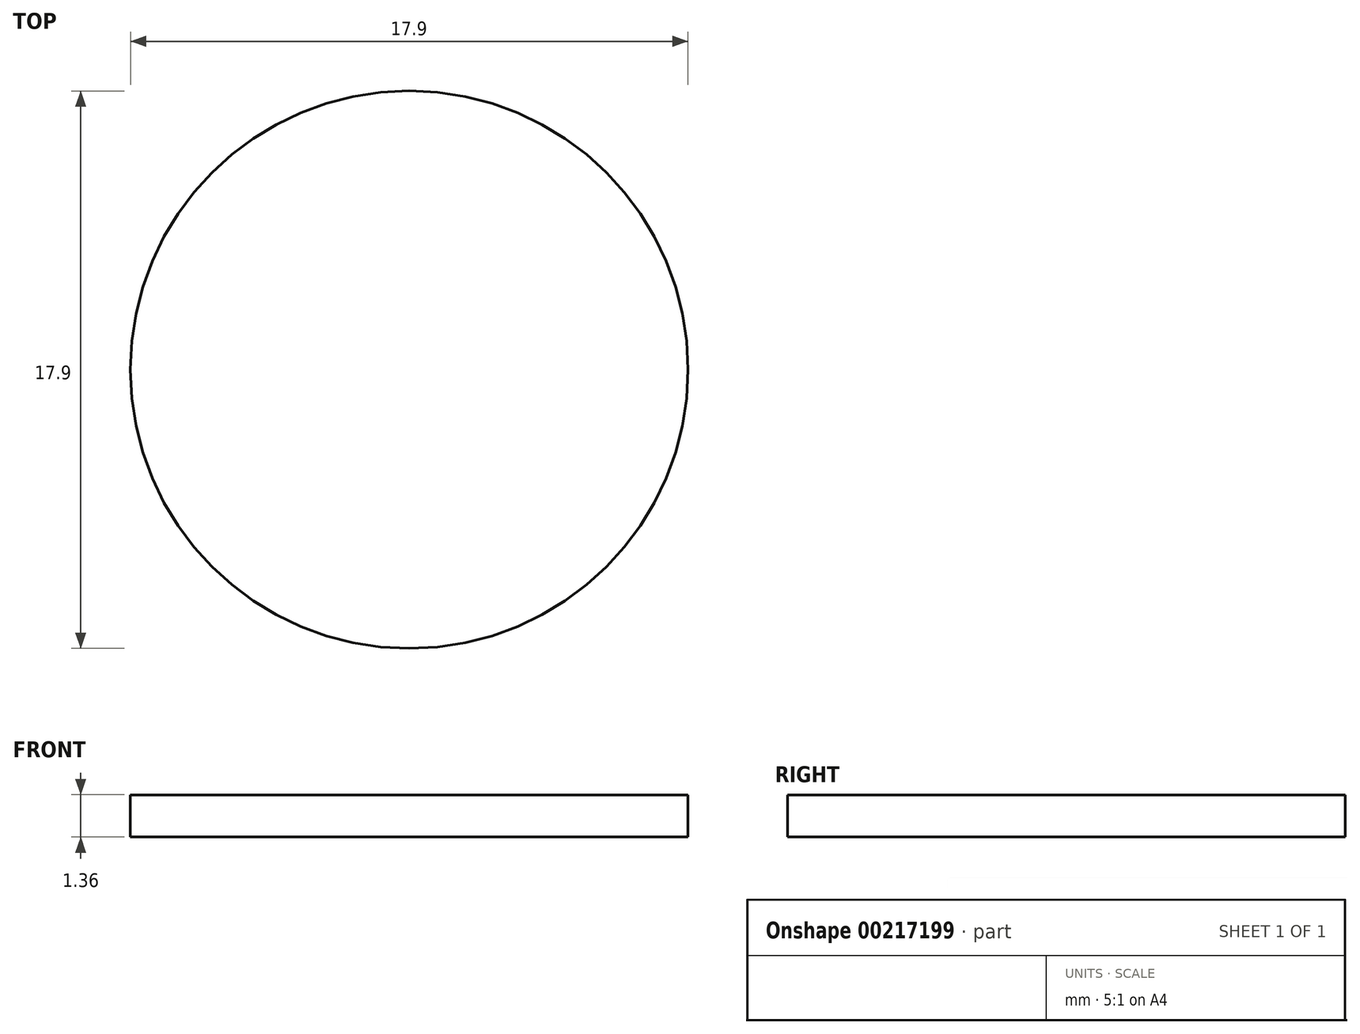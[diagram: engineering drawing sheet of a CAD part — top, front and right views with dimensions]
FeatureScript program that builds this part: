
annotation { "Feature Type Name" : "Feature", "Feature Type Description" : "" }
export const myFeature = defineFeature(function(context is Context, id is Id, definition is map)
    precondition{}
    {
        {
            var Q0;
            Q0=qCreatedBy(makeId("Top.planeOp"),FACE);
            var sketch = newSketch(context, id + "F0", { "sketchPlane" : qUnion([Q0])});
            skCircle(sketch, "E0", {"center": v(0, 0) * mm, "radius": 8.95 * mm});
            skSolve(sketch);
        }
        {
            var Q0;
            Q0=qSketchRegion(id+"F0",true);
            extrude(context, id + "F1", {"entities" : qUnion([Q0]), "endBound" : BoundingType.SYMMETRIC, "depth" : 1.35 * mm});
        }
    });
